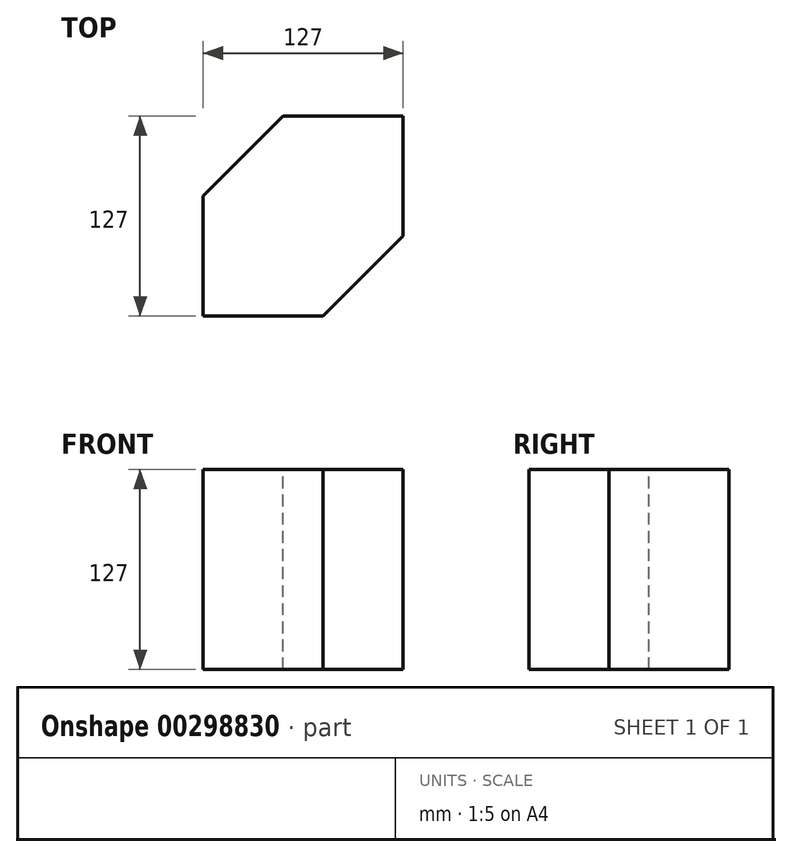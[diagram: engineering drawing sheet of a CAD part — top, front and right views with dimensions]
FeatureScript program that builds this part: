
annotation { "Feature Type Name" : "Feature", "Feature Type Description" : "" }
export const myFeature = defineFeature(function(context is Context, id is Id, definition is map)
    precondition{}
    {
        {
            var Q0;
            Q0=qCreatedBy(makeId("Top.planeOp"),FACE);
            var sketch = newSketch(context, id + "F0", { "sketchPlane" : qUnion([Q0])});
            skLineSegment(sketch, "E0.bottom", {"start": v(-63.5, 63.5) * mm, "end": v(63.5, 63.5) * mm});
            skLineSegment(sketch, "E0.top", {"start": v(-63.5, -63.5) * mm, "end": v(63.5, -63.5) * mm});
            skLineSegment(sketch, "E0.left", {"start": v(-63.5, 63.5) * mm, "end": v(-63.5, -63.5) * mm});
            skLineSegment(sketch, "E0.right", {"start": v(63.5, 63.5) * mm, "end": v(63.5, -63.5) * mm});
            skPoint(sketch, "E0.middle", {"position": v(0, 0) * mm});
            skSolve(sketch);
        }
        {
            var Q0;
            Q0=makeQuery(id+"F0.imprint","IMPRINT",FACE,{"disambiguationData":[TD([[makeQuery(id+"F0.imprint","IMPRINT",EDGE,{"derivedFrom":sQuery(id+"F0.wireOp",EDGE,"E0.bottom")}),-1.0]])]});
            extrude(context, id + "F1", {"entities" : qUnion([Q0]), "depth" : 101.6 * mm});
        }
        {
            var Q0;
            Q0=makeQuery(id+"F1.opExtrude","CAP_FACE",FACE,{"disambiguationData":[OSD([sQuery(id+"F0.wireOp",EDGE,"E0.bottom"),sQuery(id+"F0.wireOp",EDGE,"E0.top"),sQuery(id+"F0.wireOp",EDGE,"E0.left"),sQuery(id+"F0.wireOp",EDGE,"E0.right")])],"isStart":false});
            var sketch = newSketch(context, id + "F2", { "sketchPlane" : qUnion([Q0])});
            skLineSegment(sketch, "E1", {"start": v(-63.5, 63.5) * mm, "end": v(-12.7, 63.5) * mm});
            skLineSegment(sketch, "E2", {"start": v(-63.5, 63.5) * mm, "end": v(-63.5, 12.7) * mm});
            skLineSegment(sketch, "E3", {"start": v(-12.7, 63.5) * mm, "end": v(-63.5, 12.7) * mm});
            skLineSegment(sketch, "E4", {"start": v(63.5, -63.5) * mm, "end": v(63.5, -12.7) * mm});
            skLineSegment(sketch, "E5", {"start": v(63.5, -63.5) * mm, "end": v(12.7, -63.5) * mm});
            skLineSegment(sketch, "E6", {"start": v(63.5, -12.7) * mm, "end": v(12.7, -63.5) * mm});
            skSolve(sketch);
        }
        {
            var Q0;
            Q0=makeQuery(id+"F2.imprint","IMPRINT",FACE,{"disambiguationData":[TD([[makeQuery(id+"F2.imprint","IMPRINT",EDGE,{"derivedFrom":sQuery(id+"F2.wireOp",EDGE,"E1")}),-1.0]])]});
            var Q1;
            Q1=makeQuery(id+"F2.imprint","IMPRINT",FACE,{"disambiguationData":[TD([[makeQuery(id+"F2.imprint","IMPRINT",EDGE,{"derivedFrom":sQuery(id+"F2.wireOp",EDGE,"E4")}),-1.0]])]});
            extrude(context, id + "F3", {"entities" : qUnion([Q0, Q1]), "operationType" : NewBodyOperationType.REMOVE, "oppositeDirection" : true, "depth" : 101.6 * mm});
        }
        {
            var Q0;
            Q0=makeQuery(id+"F1.opExtrude","CAP_FACE",FACE,{"disambiguationData":[OSD([sQuery(id+"F0.wireOp",EDGE,"E0.bottom"),sQuery(id+"F0.wireOp",EDGE,"E0.top"),sQuery(id+"F0.wireOp",EDGE,"E0.left"),sQuery(id+"F0.wireOp",EDGE,"E0.right")])],"isStart":false});
            extrude(context, id + "F4", {"entities" : qUnion([Q0]), "operationType" : NewBodyOperationType.ADD, "depth" : 25.4 * mm});
        }
    });
